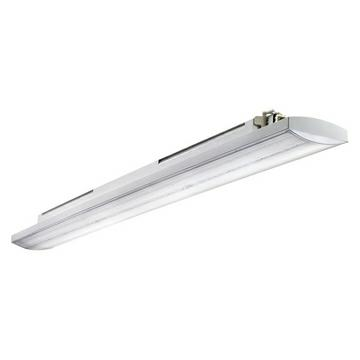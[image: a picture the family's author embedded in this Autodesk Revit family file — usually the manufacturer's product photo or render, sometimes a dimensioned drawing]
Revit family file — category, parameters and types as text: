
# Revit family: Lighting-Industriale-GEWISS-SMART[3]PLUS-HLO-PLAFONIERA-LED_TRANSPARENTE_1600mm
name_source: partatom
category: Apparecchi per illuminazione
units: mm (PartAtom-declared; Revit-internal decimal feet)

## family parameters
Condiviso = No
Host = Superficie
Punto di calcolo locali = No
Quota connettore circolare = Usa diametro
Sorgente d'illuminazione = Sì
Taglio con vuoti quando caricato = No
Tipo di parte = Normale

## types (1)
- Lighting-Industriale-GEWISS-SMART[3]PLUS-HLO-PLAFONIERA-LED_TRANSPARENTE_1600mm
    Angolo inclinazione = -90.00°
    Applicazione = Interno
    Carico apparente = 67 VA
    Catalogo = LIGHTING
    Catalogo Serie = SMART[3] PLUS HLO
    Classe di efficienza LED integrati = A ÷ A++
    Classe isolamento = II
    Codice Electrocod = 2434
    Commenti sul wattaggio = 67W
    Descrizione = SMART3 PLUS 1600 T.W.DALI HO TRASP 9 57
    Emetti da lunghezza linea = 1200 mm
    File diagramma fotometrico = GWS3323BT957.IES
    Filtro dei colori = 16777215
    Ganci = Alluminio
    Garanzia = 5 anni
    Glow Wire Test = 850°C
    Grado di protezione = IP66/IP69
    IDF = 7ec288e1-885b-4a9d-ba83-87dd9d071491
    IDT = a13ebeb2-bfa1-469e-9c7f-0ca841da0dbd
    Immagine tipo = GWS3280TS.jpg
    Lampada = LED
    Lampada: = LED
    Lumen output (lm) = 7400
    Lunghezza = 1600 mm
    Lunghezza Lampada = 1600 mm  [stored 5.24934 ft]
    Modello = GWS3323BT957
    Numero poli = 2
    Potenza di sistema = 63 W
    Produttore = GEWISS S.p.A.
    Prospetto di default = 1219 mm
    Resistenza agli urti = IK08
    SEO = Plafoniera
    Scheda Tecnica = https://www.gewiss.com
    Schermo = Trasparente
    Schermo. = Led Acceso
    Stampa 1_100 = Sì
    Stampa 1_200 = No
    Struttura = GRIGIO
    Temperatura di colore = 5700 K (CRI > 90)
    Temperatura di colore: = 5700 K (CRI > 90)
    Temperatura di funzionamento = -25 +45 °C
    Temperatura di utilizzo = -25 +45 °C
    Tensione = 220-240 V
    Tipologia = DALI
    Tipologia sorgente luminosa = LED - Non sostituibile
    URL = https://www.gewiss.com
    Variazione temperatura colore lampada con luminosità attenuata = <Nessuno>
    Versione file RFA = 20.0

note: [stored X ft] marks values corroborated as IEEE doubles in the binary element streams (Revit-internal decimal feet)
